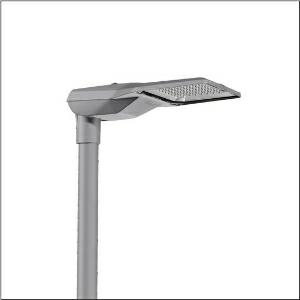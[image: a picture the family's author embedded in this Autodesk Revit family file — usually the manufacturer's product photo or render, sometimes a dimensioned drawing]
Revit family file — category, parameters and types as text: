
# Revit family: streetlight_sl_21_midi___st0_8a_5xe3c43s08lb_4b77
name_source: partatom
category: Lighting Fixtures
units: mm (PartAtom-declared; Revit-internal decimal feet)

## family parameters
Cut with Voids When Loaded = No
Host = Face
Light Source = No
Part Type = Normal
Room Calculation Point = No
Round Connector Dimension = Use Diameter
Shared = No

## types (1)
- --- (1 x LED, 14950 lm, 99.6 W, 4000K)
    Apparent Load = 100 VA
    CIE Flux Codes = 38 75 97 100 100
    Color Rendering = 70
    Color Temperature = 4000K
    Default Elevation = 1800 mm
    Description = Streetlight SL 21 midi, mast luminaire, primary light control with lens, of PMMA, primary optical cover: cover, of toughened safety glass, transparent, light distribution: ST0.8a, light emission: direct distribution, primary light characteristic: asymmetric, installation type: side-entry, post-top, LED, High Power LED, rated luminous flux: 14.950lm, luminous efficacy: 150lm/W, light colour: 740, colour temperature: 4000K, control gear: D4i, control: overheat protection, constant luminous flux control, time-dependent luminous flux control, flexible luminous flux parameterisation, pre-setting: logarithmic dimming characteristic, mains connection: 230..240V, AC, 50/60Hz, start of lifetime: 100W, end of service life: 102W, reduction: 46W, luminaire housing, of diecast aluminium, powder-coated, Siteco® metallic grey (DB 702S), corrosivity category C5 mid according to DIN EN ISO 12944, please order mast flange separately, inclination adjustable: 0°, 5°, 10°, 15°, sealing non-destructively replaceable, multi-level sealing system, length: 644mm, width: 335mm, height: 110mm, mast flange for spigot size: 42mm (side-entry): 5XC10008XM4, 60/48mm (side-entry/post-top): 5XC10108XM2, 76/60mm (side-entry/post-top): 5XC10108XM1, mounting height: 4..8m, Smart Interface above, protection rating (complete): IP66, insulation class (complete): insulation class II (safety insulation), certification: CE, ENEC, ENEC+, VDE, impact resistance: IK10, permissible operating ambient temperature for outdoor applications: -40..+50°C, standard-compliant lighting for roads and squares, packaging unit: 1 piece

Light Distribution: ST0.8a
    Height = 111 mm
    Lamp = 1 x LED
    Lamp Light Flux = 14950 lm
    Lamp Power = 99.6 W
    Lamp count = 1
    Length = 644 mm
    Luminous efficacy = 150 lm/W
    Manufacturer = Siteco
    ModVariant = No
    Model = 5XE3C43S08LB
    Number of Poles = 1
    OnlyDefault = Yes
    Power Factor = 1
    Product Name = Streetlight SL 21 midi | ST0.8a
    Product group = mast luminaire | pylon top
    ProductGroupID = 6100
    Protection Class = Protection class II
    Protection Degree = IP 66
    RLX_Detail_Level = 1
    RLX_Emergency_Light_Flux = 0 lm
    RLX_Emergency_Type = 0
    RLX_Emergency_Type_DB = No
    RlxData = <blob elided: 26821 chars, md5=31bcd8d6>
    Socket = socket
    Standby Power = 0 W
    System Light Flux = 14950 lm
    System Power = 100 W
    Type Comments = factory setting: luminous flux: 100 % | dim-lin: 254 | 1020 mA
    Type Image = l_1004302.jpg
    URL = http://relux.com
    VarID = @adj_031287
    Voltage = 0 V
    Weight = 0.00 kg
    Width = 336 mm

## geometry (parser evidence)
native form markers: Blend x4, Sweep x11
no freeform markers — native parametric forms only
